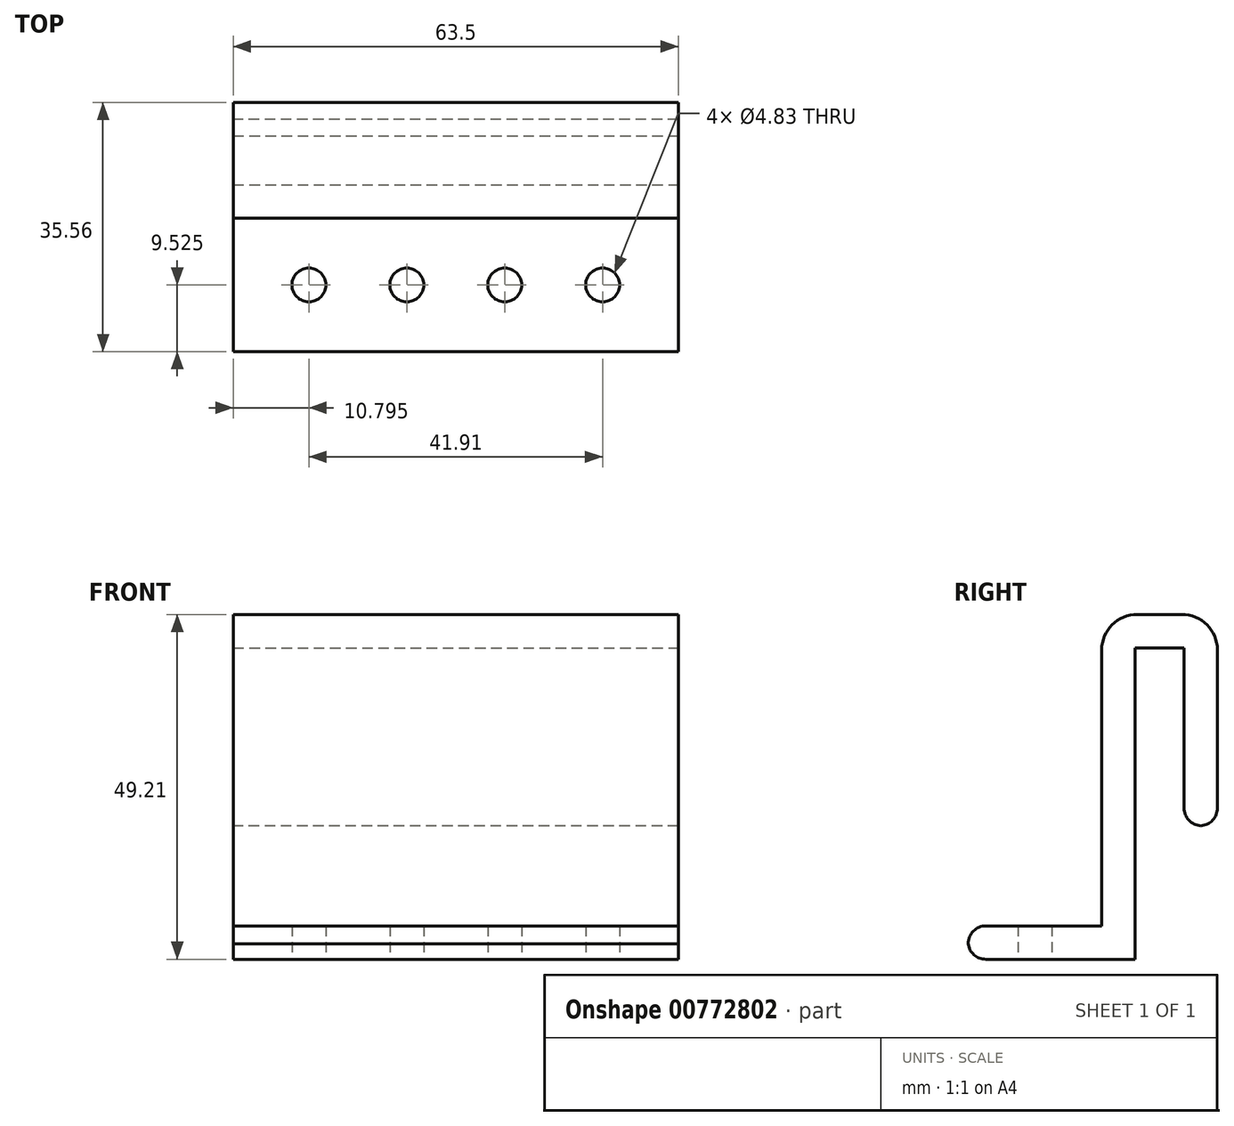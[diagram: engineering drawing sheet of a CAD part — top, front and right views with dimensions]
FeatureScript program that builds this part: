
annotation { "Feature Type Name" : "Feature", "Feature Type Description" : "" }
export const myFeature = defineFeature(function(context is Context, id is Id, definition is map)
    precondition{}
    {
        {
            var Q0;
            Q0=qCreatedBy(makeId("Front.planeOp"),FACE);
            var sketch = newSketch(context, id + "F0", { "sketchPlane" : qUnion([Q0])});
            skLineSegment(sketch, "E0.bottom", {"start": v(-63.5, 0) * mm, "end": v(0, 0) * mm});
            skLineSegment(sketch, "E0.top", {"start": v(-63.5, -25.4) * mm, "end": v(0, -25.4) * mm});
            skLineSegment(sketch, "E0.left", {"start": v(-63.5, 0) * mm, "end": v(-63.5, -25.4) * mm});
            skLineSegment(sketch, "E0.right", {"start": v(0, 0) * mm, "end": v(0, -25.4) * mm});
            skSolve(sketch);
        }
        {
            var Q0;
            Q0=makeQuery(id+"F0.imprint","IMPRINT",FACE,{"disambiguationData":[TD([[makeQuery(id+"F0.imprint","IMPRINT",EDGE,{"derivedFrom":sQuery(id+"F0.wireOp",EDGE,"E0.bottom")}),-1.0]])]});
            extrude(context, id + "F1", {"entities" : qUnion([Q0]), "depth" : 4.76 * mm, "offsetDistance" : 25.4 * mm});
        }
        {
            var Q0;
            Q0=qCreatedBy(makeId("Top.planeOp"),FACE);
            var sketch = newSketch(context, id + "F2", { "sketchPlane" : qUnion([Q0])});
            skLineSegment(sketch, "E1.bottom", {"start": v(0, 0) * mm, "end": v(-63.5, 0) * mm});
            skLineSegment(sketch, "E1.top", {"start": v(0, -16.5) * mm, "end": v(-63.5, -16.51) * mm});
            skLineSegment(sketch, "E1.left", {"start": v(0, 0) * mm, "end": v(0, -16.5) * mm});
            skLineSegment(sketch, "E1.right", {"start": v(-63.5, 0) * mm, "end": v(-63.5, -16.51) * mm});
            skSolve(sketch);
        }
        {
            var Q0;
            Q0 = qSketchRegion(id + "F2", true);
            extrude(context, id + "F3", {"entities" : qUnion([Q0]), "operationType" : NewBodyOperationType.ADD, "depth" : 4.76 * mm, "offsetDistance" : 25.4 * mm});
        }
        {
            var Q0;
            Q0=qCreatedBy(makeId("Right.planeOp"),FACE);
            var sketch = newSketch(context, id + "F4", { "sketchPlane" : qUnion([Q0])});
            skLineSegment(sketch, "E2.bottom", {"start": v(-16.5, 0) * mm, "end": v(-11.75, 0) * mm});
            skLineSegment(sketch, "E2.top", {"start": v(-16.5, -44.45) * mm, "end": v(-11.75, -44.45) * mm});
            skLineSegment(sketch, "E2.left", {"start": v(-16.5, 0) * mm, "end": v(-16.5, -44.45) * mm});
            skLineSegment(sketch, "E2.right", {"start": v(-11.75, 0) * mm, "end": v(-11.75, -44.45) * mm});
            skSolve(sketch);
        }
        {
            var Q0;
            Q0=makeQuery(id+"F4.imprint","IMPRINT",FACE,{"disambiguationData":[TD([[makeQuery(id+"F4.imprint","IMPRINT",EDGE,{"derivedFrom":sQuery(id+"F4.wireOp",EDGE,"E2.bottom")}),-1.0]])]});
            extrude(context, id + "F5", {"entities" : qUnion([Q0]), "operationType" : NewBodyOperationType.ADD, "oppositeDirection" : true, "depth" : 63.5 * mm, "offsetDistance" : 25.4 * mm});
        }
        {
            var Q0;
            Q0=qCreatedBy(makeId("Right.planeOp"),FACE);
            var sketch = newSketch(context, id + "F6", { "sketchPlane" : qUnion([Q0])});
            skLineSegment(sketch, "E3.bottom", {"start": v(-16.5, -44.45) * mm, "end": v(-35.56, -44.45) * mm});
            skLineSegment(sketch, "E3.top", {"start": v(-16.5, -39.69) * mm, "end": v(-35.56, -39.69) * mm});
            skLineSegment(sketch, "E3.left", {"start": v(-16.5, -44.45) * mm, "end": v(-16.5, -39.69) * mm});
            skLineSegment(sketch, "E3.right", {"start": v(-35.56, -44.45) * mm, "end": v(-35.56, -39.69) * mm});
            skSolve(sketch);
        }
        {
            var Q0;
            Q0=makeQuery(id+"F6.imprint","IMPRINT",FACE,{"disambiguationData":[TD([[makeQuery(id+"F6.imprint","IMPRINT",EDGE,{"derivedFrom":sQuery(id+"F6.wireOp",EDGE,"E3.bottom")}),-1.0]])]});
            extrude(context, id + "F7", {"entities" : qUnion([Q0]), "operationType" : NewBodyOperationType.ADD, "oppositeDirection" : true, "depth" : 63.5 * mm, "offsetDistance" : 25.4 * mm});
        }
        {
            var Q0;
            Q0=makeQuery(id+"F7.boolean.opBoolean","MERGE",FACE,{"derivedFrom":[makeQuery(id+"F5.opExtrude","SWEPT_FACE",FACE,{"disambiguationData":[OSD([sQuery(id+"F4.wireOp",EDGE,"E2.top")])]}),makeQuery(id+"F7.opExtrude","SWEPT_FACE",FACE,{"disambiguationData":[OSD([sQuery(id+"F6.wireOp",EDGE,"E3.bottom")])]})]});
            var sketch = newSketch(context, id + "F8", { "sketchPlane" : qUnion([Q0])});
            skCircle(sketch, "E4", {"center": v(-52.7, 26.03) * mm, "radius": 2.41 * mm});
            skCircle(sketch, "E5", {"center": v(-38.74, 26.04) * mm, "radius": 2.41 * mm});
            skCircle(sketch, "E6", {"center": v(-24.77, 26.04) * mm, "radius": 2.41 * mm});
            skCircle(sketch, "E7", {"center": v(-10.8, 26.04) * mm, "radius": 2.41 * mm});
            skSolve(sketch);
        }
        {
            var Q0;
            Q0=makeQuery(id+"F8.imprint","IMPRINT",FACE,{"disambiguationData":[TD([[makeQuery(id+"F8.imprint","IMPRINT",EDGE,{"derivedFrom":sQuery(id+"F8.wireOp",EDGE,"E4")}),1.0]])]});
            var Q1;
            Q1=makeQuery(id+"F8.imprint","IMPRINT",FACE,{"disambiguationData":[TD([[makeQuery(id+"F8.imprint","IMPRINT",EDGE,{"derivedFrom":sQuery(id+"F8.wireOp",EDGE,"E5")}),1.0]])]});
            var Q2;
            Q2=makeQuery(id+"F8.imprint","IMPRINT",FACE,{"disambiguationData":[TD([[makeQuery(id+"F8.imprint","IMPRINT",EDGE,{"derivedFrom":sQuery(id+"F8.wireOp",EDGE,"E6")}),1.0]])]});
            var Q3;
            Q3=makeQuery(id+"F8.imprint","IMPRINT",FACE,{"disambiguationData":[TD([[makeQuery(id+"F8.imprint","IMPRINT",EDGE,{"derivedFrom":sQuery(id+"F8.wireOp",EDGE,"E7")}),1.0]])]});
            extrude(context, id + "F9", {"entities" : qUnion([Q0, Q1, Q2, Q3]), "operationType" : NewBodyOperationType.REMOVE, "oppositeDirection" : true, "depth" : 4.76 * mm, "offsetDistance" : 25.4 * mm});
        }
        {
            var Q0;
            Q0=makeQuery(id+"F3.opExtrude","CAP_EDGE",EDGE,{"disambiguationData":[OSD([sQuery(id+"F2.wireOp",EDGE,"E1.bottom")])],"isStart":false});
            var Q1;
            Q1=makeQuery(id+"F3.opExtrude","CAP_EDGE",EDGE,{"disambiguationData":[OSD([sQuery(id+"F2.wireOp",EDGE,"E1.top")])],"isStart":false});
            fillet(context, id + "F10", {"entities" : qUnion([Q0, Q1]), "radius" : 5.08 * mm, "tangentPropagation" : true, "allowEdgeOverflow" : false});
        }
        {
            var Q0;
            Q0=makeQuery(id+"F7.opExtrude","SWEPT_EDGE",EDGE,{"disambiguationData":[OSD([sQuery(id+"F6.wireOp",EDGE,"E3.top"),sQuery(id+"F6.wireOp",EDGE,"E3.right")])]});
            fillet(context, id + "F11", {"entities" : qUnion([Q0]), "radius" : 2.54 * mm, "tangentPropagation" : true, "allowEdgeOverflow" : false});
        }
        {
            var Q0;
            Q0=makeQuery(id+"F1.opExtrude","CAP_EDGE",EDGE,{"disambiguationData":[OSD([sQuery(id+"F0.wireOp",EDGE,"E0.top")])],"isStart":false});
            var Q1;
            Q1=makeQuery(id+"F1.opExtrude","CAP_EDGE",EDGE,{"disambiguationData":[OSD([sQuery(id+"F0.wireOp",EDGE,"E0.top")])],"isStart":true});
            fillet(context, id + "F12", {"entities" : qUnion([Q0, Q1]), "radius" : 2.54 * mm, "tangentPropagation" : true, "allowEdgeOverflow" : false});
        }
        {
            var Q0;
            Q0=makeQuery(id+"F7.opExtrude","SWEPT_EDGE",EDGE,{"disambiguationData":[OSD([sQuery(id+"F6.wireOp",EDGE,"E3.bottom"),sQuery(id+"F6.wireOp",EDGE,"E3.right")])]});
            fillet(context, id + "F13", {"entities" : qUnion([Q0]), "radius" : 2.54 * mm, "tangentPropagation" : true, "allowEdgeOverflow" : false});
        }
    });
